# Revit family: Shower-Shower_Door-KOHLER-TRILGOY-K-72922T_2
name_source: partatom
category: Specialty Equipment
revit_build: Autodesk Revit 2017 (Build: 20160225_1515(x64)
units: mm (PartAtom-declared; Revit-internal decimal feet)

## family parameters
Cut with Voids When Loaded = No
Host = Face
OmniClass Number = 23.31.17.17
OmniClass Title = Shower Enclosures
Part Type = Normal
Room Calculation Point = No
Round Connector Dimension = Use Diameter
Shared = No

## types (2) — shared parameters
ADA Compliant = No
Assembly Code = C1030200
Date Modified = 08/24/2020
Default Elevation = 0"
Description = Hinge screen, 1 door 1 panel, 8mm thick glass
Height = 77 3/16"
Length = 5 1/4"
Manufacturer = KOHLER Co.
Master Format 2014 = 10 28 19.16
Master Format 2014 Name = Shower Doors
Material = Premium Metal Construction
Product Name = TRILGOY
URL = http://www.kohler.com.cn
WaterSense Certified = No
Width = 47 5/8"

## per-type parameters (varying)
| type | Finish | Model | Type |
| SHP-Polished Bright Silver | Kohler-Metal-SHP-Bright_Polished_Silver | K-72922T-L-SHP | 1 |
| 2BL-Original Black | Kohler-Metal-2BL-Original_Black | K-72922T-L-2BL | 2 |

## geometry (parser evidence)
native form markers: Sweep x5
no freeform markers — native parametric forms only
